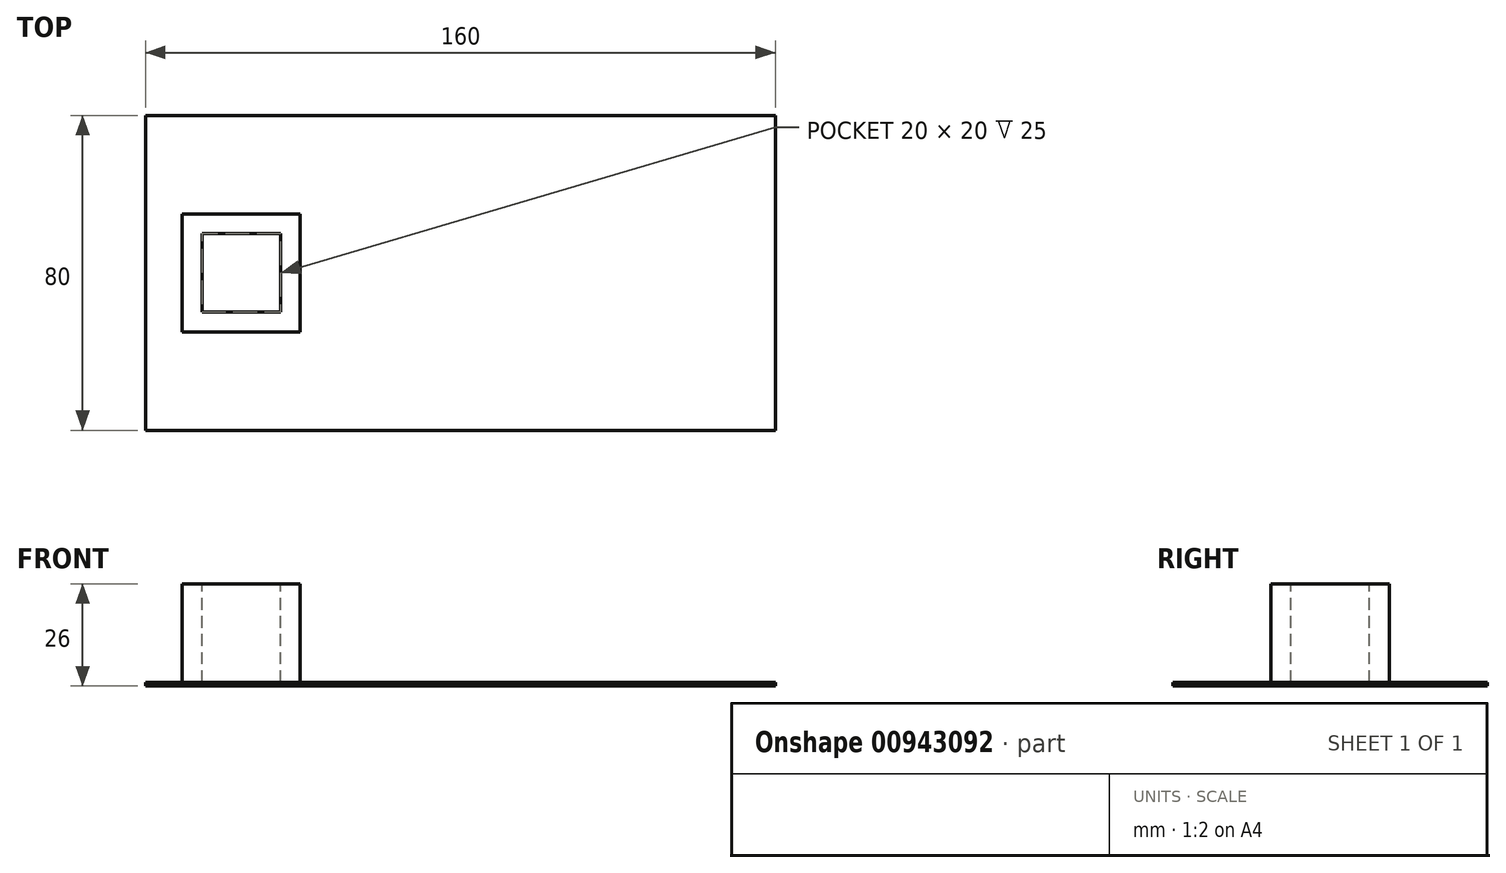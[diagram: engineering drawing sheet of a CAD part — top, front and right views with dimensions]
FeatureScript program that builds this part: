
annotation { "Feature Type Name" : "Feature", "Feature Type Description" : "" }
export const myFeature = defineFeature(function(context is Context, id is Id, definition is map)
    precondition{}
    {
        {
            var Q0;
            Q0=qCreatedBy(makeId("Top.planeOp"),FACE);
            var sketch = newSketch(context, id + "F0", { "sketchPlane" : qUnion([Q0])});
            skLineSegment(sketch, "E0.bottom", {"start": v(-80, 40) * mm, "end": v(80, 40) * mm});
            skLineSegment(sketch, "E0.top", {"start": v(-80, -40) * mm, "end": v(80, -40) * mm});
            skLineSegment(sketch, "E0.left", {"start": v(-80, 40) * mm, "end": v(-80, -40) * mm});
            skLineSegment(sketch, "E0.right", {"start": v(80, 40) * mm, "end": v(80, -40) * mm});
            skLineSegment(sketch, "E1", {"start": v(80, 40) * mm, "end": v(-80, -40) * mm, "construction": true});
            skPoint(sketch, "E2", {"position": v(0, 0) * mm});
            skSolve(sketch);
        }
        {
            var Q0;
            Q0 = qSketchRegion(id + "F0", true);
            extrude(context, id + "F1", {"entities" : qUnion([Q0]), "depth" : 1 * mm, "offsetDistance" : 25 * mm});
        }
        {
            var Q0;
            Q0=makeQuery(id+"F1.opExtrude","CAP_FACE",FACE,{"disambiguationData":[OSD([sQuery(id+"F0.wireOp",EDGE,"E0.bottom"),sQuery(id+"F0.wireOp",EDGE,"E0.top"),sQuery(id+"F0.wireOp",EDGE,"E0.left"),sQuery(id+"F0.wireOp",EDGE,"E0.right")])],"isStart":false});
            var sketch = newSketch(context, id + "F2", { "sketchPlane" : qUnion([Q0])});
            skLineSegment(sketch, "E3.bottom", {"start": v(-70.68, 15) * mm, "end": v(-40.68, 15) * mm});
            skLineSegment(sketch, "E3.top", {"start": v(-70.68, -15) * mm, "end": v(-40.68, -15) * mm});
            skLineSegment(sketch, "E3.left", {"start": v(-70.68, 15) * mm, "end": v(-70.68, -15) * mm});
            skLineSegment(sketch, "E3.right", {"start": v(-40.68, 15) * mm, "end": v(-40.68, -15) * mm});
            skPoint(sketch, "E4", {"position": v(-40.68, 0) * mm});
            skSolve(sketch);
        }
        {
            var Q0;
            Q0 = qSketchRegion(id + "F2", true);
            extrude(context, id + "F3", {"entities" : qUnion([Q0]), "operationType" : NewBodyOperationType.ADD, "depth" : 25 * mm, "offsetDistance" : 25 * mm});
        }
        {
            var Q0;
            Q0=makeQuery(id+"F3.opExtrude","CAP_FACE",FACE,{"disambiguationData":[OSD([sQuery(id+"F2.wireOp",EDGE,"E3.bottom"),sQuery(id+"F2.wireOp",EDGE,"E3.top"),sQuery(id+"F2.wireOp",EDGE,"E3.left"),sQuery(id+"F2.wireOp",EDGE,"E3.right")])],"isStart":false});
            var sketch = newSketch(context, id + "F4", { "sketchPlane" : qUnion([Q0])});
            skLineSegment(sketch, "E5", {"start": v(-70.68, 15) * mm, "end": v(-40.68, -15) * mm, "construction": true});
            skLineSegment(sketch, "E6.bottom", {"start": v(-45.68, -10) * mm, "end": v(-65.68, -10) * mm});
            skLineSegment(sketch, "E6.top", {"start": v(-45.68, 10) * mm, "end": v(-65.68, 10) * mm});
            skLineSegment(sketch, "E6.left", {"start": v(-45.68, -10) * mm, "end": v(-45.68, 10) * mm});
            skLineSegment(sketch, "E6.right", {"start": v(-65.68, -10) * mm, "end": v(-65.68, 10) * mm});
            skPoint(sketch, "E6.middle", {"position": v(-55.68, 0) * mm});
            skSolve(sketch);
        }
        {
            var Q0;
            Q0 = qSketchRegion(id + "F4", true);
            extrude(context, id + "F5", {"entities" : qUnion([Q0]), "operationType" : NewBodyOperationType.REMOVE, "oppositeDirection" : true, "depth" : 25 * mm, "offsetDistance" : 25 * mm});
        }
    });
